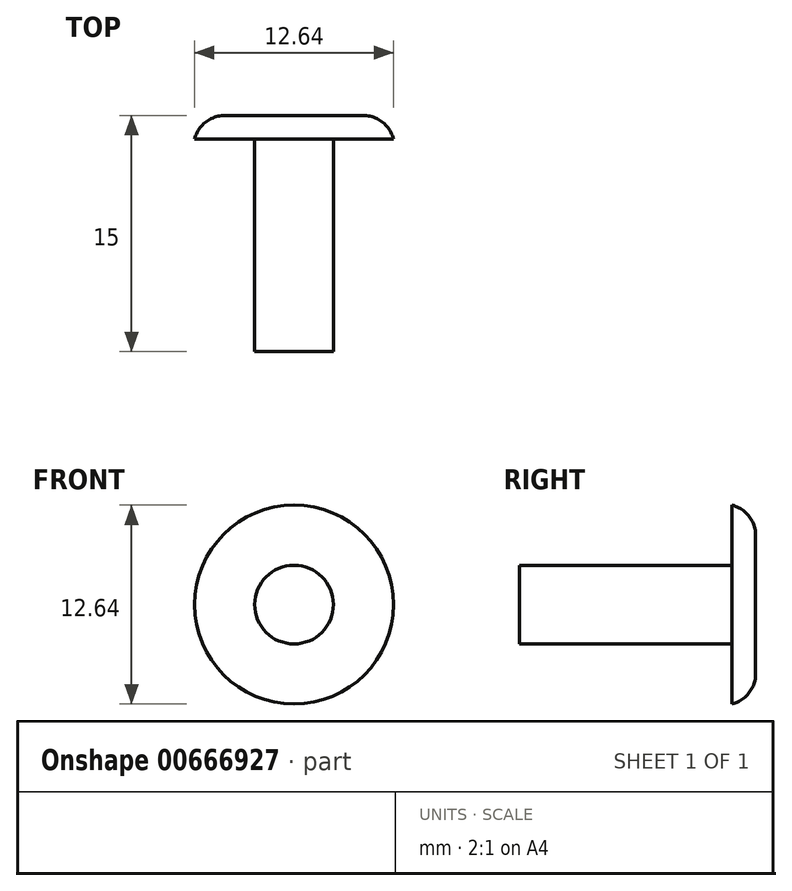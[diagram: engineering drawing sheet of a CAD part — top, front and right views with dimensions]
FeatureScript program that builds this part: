
annotation { "Feature Type Name" : "Feature", "Feature Type Description" : "" }
export const myFeature = defineFeature(function(context is Context, id is Id, definition is map)
    precondition{}
    {
        {
            var Q0;
            Q0=qCreatedBy(makeId("Front.planeOp"),FACE);
            var sketch = newSketch(context, id + "F0", { "sketchPlane" : qUnion([Q0])});
            skCircle(sketch, "E0", {"center": v(0, 0) * mm, "radius": 6.32 * mm});
            skCircle(sketch, "E1", {"center": v(0, 0) * mm, "radius": 2.5 * mm});
            skSolve(sketch);
        }
        {
            var Q0;
            Q0=makeQuery(id+"F0.imprint","IMPRINT",FACE,{"disambiguationData":[TD([[makeQuery(id+"F0.imprint","IMPRINT",EDGE,{"derivedFrom":sQuery(id+"F0.wireOp",EDGE,"E1")}),1.0]])]});
            var Q1;
            Q1=sQuery(id+"F0.wireOp",EDGE,"E1");
            extrude(context, id + "F1", {"entities" : qUnion([Q0]), "surfaceEntities" : qUnion([Q1]), "depth" : 15 * mm, "offsetDistance" : 25 * mm});
        }
        {
            var Q0;
            Q0 = qSketchRegion(id + "F0", true);
            extrude(context, id + "F2", {"entities" : qUnion([Q0]), "operationType" : NewBodyOperationType.ADD, "depth" : 1.5 * mm, "offsetDistance" : 25 * mm});
        }
        {
            var Q0;
            {var subQ0=sQuery(id+"F0.wireOp",EDGE,"E1");Q0=makeQuery(id+"F2.boolean.opBoolean","MERGE",FACE,{"derivedFrom":[makeQuery(id+"F1.opExtrude","CAP_FACE",FACE,{"disambiguationData":[OSD([subQ0])],"isStart":true}),makeQuery(id+"F2.opExtrude","CAP_FACE",FACE,{"disambiguationData":[OSD([sQuery(id+"F0.wireOp",EDGE,"E0"),subQ0])],"isStart":true})]});}
            fillet(context, id + "F3", {"entities" : qUnion([Q0]), "radius" : 2 * mm, "tangentPropagation" : true, "allowEdgeOverflow" : false});
        }
    });
